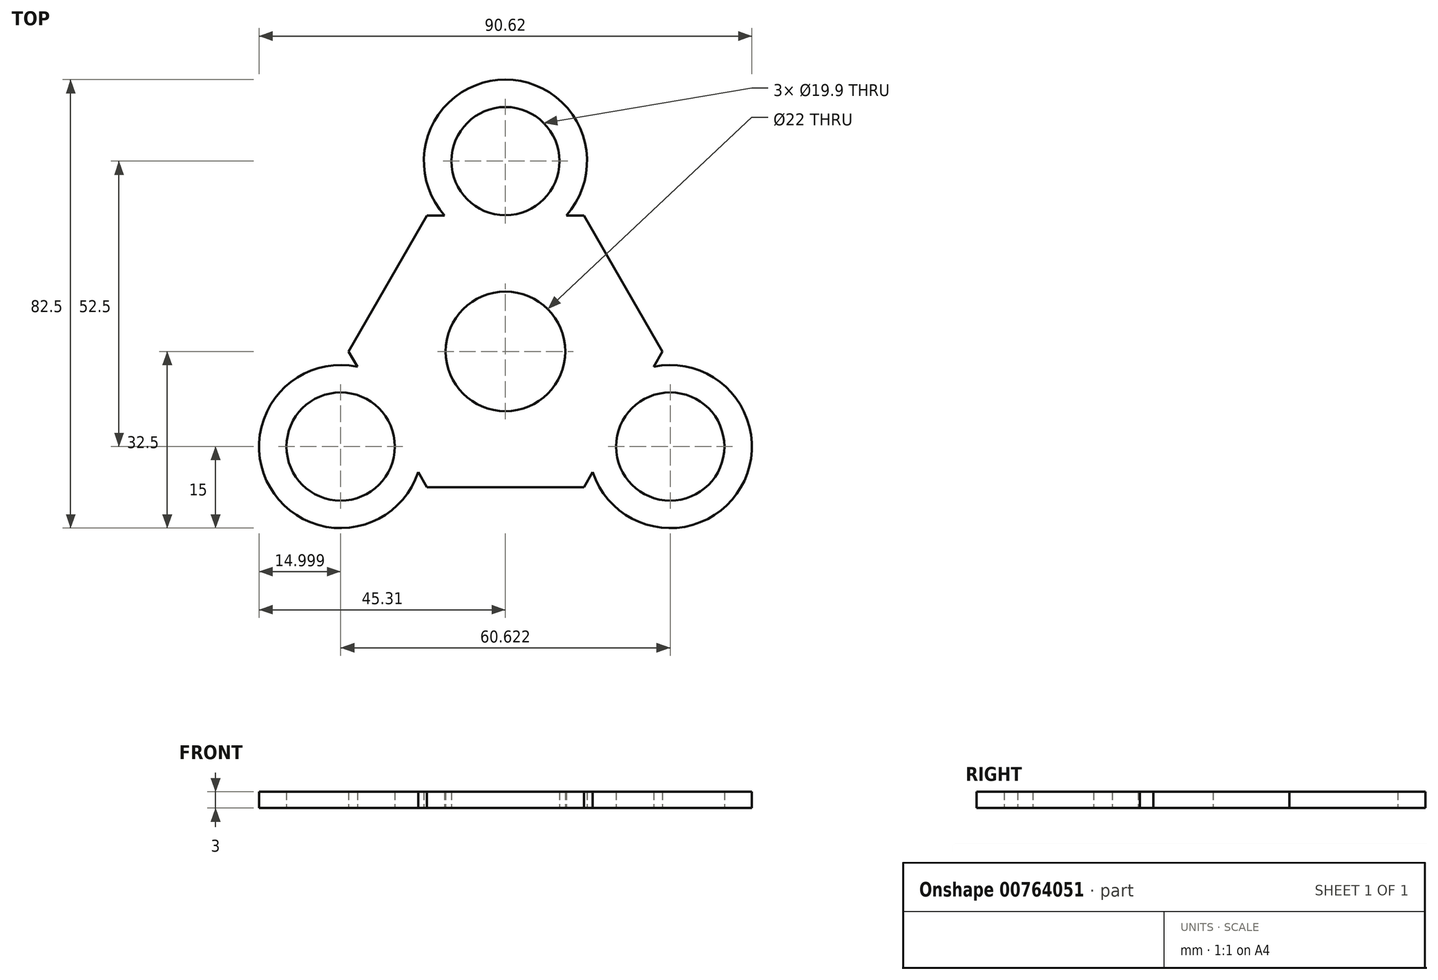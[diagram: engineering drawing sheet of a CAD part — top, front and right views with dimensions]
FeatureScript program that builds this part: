
annotation { "Feature Type Name" : "Feature", "Feature Type Description" : "" }
export const myFeature = defineFeature(function(context is Context, id is Id, definition is map)
    precondition{}
    {
        {
            var Q0;
            Q0=qCreatedBy(makeId("Top.planeOp"),FACE);
            var sketch = newSketch(context, id + "F0", { "sketchPlane" : qUnion([Q0])});
            skLineSegment(sketch, "E0.0", {"start": v(-14.43, 25) * mm, "end": v(-11.18, 25) * mm});
            skLineSegment(sketch, "E0.1", {"start": v(14.43, 25) * mm, "end": v(21.65, 12.5) * mm});
            skLineSegment(sketch, "E0.5", {"start": v(-21.65, 12.5) * mm, "end": v(-14.43, 25) * mm});
            skPoint(sketch, "E0.0.midPoint", {"position": v(0, 25) * mm});
            skArc(sketch, "E1", {"start": v(9.53, 5.5) * mm, "mid": v(0, 11) * mm, "end": v(-9.53, 5.5) * mm});
            skArc(sketch, "E2", {"start": v(11.18, 25) * mm, "mid": v(0, 50) * mm, "end": v(-11.18, 25) * mm});
            skCircle(sketch, "E3", {"center": v(0, 35) * mm, "radius": 9.95 * mm});
            skLineSegment(sketch, "E4.trimOffspring", {"start": v(0, 25) * mm, "end": v(0, 25.05) * mm});
            skLineSegment(sketch, "E5.trimOffspring", {"start": v(11.18, 25) * mm, "end": v(14.43, 25) * mm});
            skCircle(sketch, "E6.1.0", {"center": v(-30.31, -17.5) * mm, "radius": 9.95 * mm});
            skLineSegment(sketch, "E6.1.1", {"start": v(-28.87, 0) * mm, "end": v(-21.65, 12.5) * mm});
            skLineSegment(sketch, "E6.1.2", {"start": v(0, -25) * mm, "end": v(-14.43, -25) * mm});
            skArc(sketch, "E6.1.3", {"start": v(-27.24, -2.82) * mm, "mid": v(-43.3, -25) * mm, "end": v(-16.06, -22.18) * mm});
            skLineSegment(sketch, "E6.1.4", {"start": v(-14.43, -25) * mm, "end": v(-16.06, -22.18) * mm});
            skLineSegment(sketch, "E6.1.5", {"start": v(-27.24, -2.82) * mm, "end": v(-28.87, 0) * mm});
            skArc(sketch, "E6.1.6", {"start": v(-9.53, 5.5) * mm, "mid": v(-9.53, -5.5) * mm, "end": v(0, -11) * mm});
            skCircle(sketch, "E6.2.0", {"center": v(30.31, -17.5) * mm, "radius": 9.95 * mm});
            skLineSegment(sketch, "E6.2.1", {"start": v(14.43, -25) * mm, "end": v(0, -25) * mm});
            skLineSegment(sketch, "E6.2.2", {"start": v(21.65, 12.5) * mm, "end": v(28.87, 0) * mm});
            skArc(sketch, "E6.2.3", {"start": v(16.06, -22.18) * mm, "mid": v(43.3, -25) * mm, "end": v(27.24, -2.82) * mm});
            skLineSegment(sketch, "E6.2.4", {"start": v(28.87, 0) * mm, "end": v(27.24, -2.82) * mm});
            skLineSegment(sketch, "E6.2.5", {"start": v(16.06, -22.18) * mm, "end": v(14.43, -25) * mm});
            skArc(sketch, "E6.2.6", {"start": v(0, -11) * mm, "mid": v(9.53, -5.5) * mm, "end": v(9.53, 5.5) * mm});
            skSolve(sketch);
        }
        {
            var Q0;
            Q0 = qSketchRegion(id + "F0", true);
            extrude(context, id + "F1", {"entities" : qUnion([Q0]), "depth" : 3 * mm, "offsetDistance" : 25 * mm});
        }
    });
